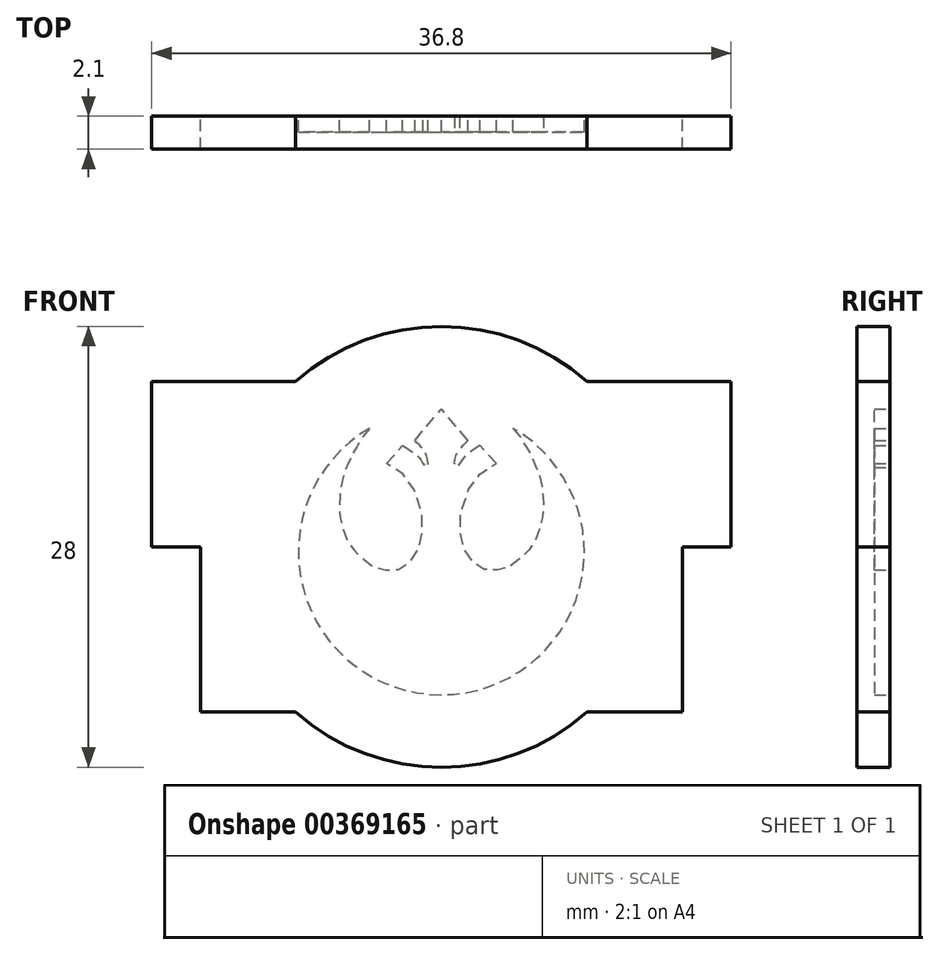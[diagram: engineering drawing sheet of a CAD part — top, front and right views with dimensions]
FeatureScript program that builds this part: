
annotation { "Feature Type Name" : "Feature", "Feature Type Description" : "" }
export const myFeature = defineFeature(function(context is Context, id is Id, definition is map)
    precondition{}
    {
        {
            var Q0;
            Q0=qCreatedBy(makeId("Front.planeOp"),FACE);
            var sketch = newSketch(context, id + "F0", { "sketchPlane" : qUnion([Q0])});
            skArc(sketch, "E0", {"start": v(-9.26, -10.5) * mm, "mid": v(0, -14) * mm, "end": v(9.26, -10.5) * mm});
            skLineSegment(sketch, "E1", {"start": v(9.26, 10.5) * mm, "end": v(18.4, 10.5) * mm});
            skLineSegment(sketch, "E2", {"start": v(18.4, 10.5) * mm, "end": v(18.4, 0) * mm});
            skLineSegment(sketch, "E3", {"start": v(18.4, 0) * mm, "end": v(15.3, 0) * mm});
            skLineSegment(sketch, "E4", {"start": v(15.3, 0) * mm, "end": v(15.3, -10.5) * mm});
            skLineSegment(sketch, "E5", {"start": v(15.3, -10.5) * mm, "end": v(9.26, -10.5) * mm});
            skLineSegment(sketch, "E6.MirrorCS", {"start": v(-18.4, 0) * mm, "end": v(-15.3, 0) * mm});
            skLineSegment(sketch, "E7.MirrorCS", {"start": v(-15.3, 0) * mm, "end": v(-15.3, -10.5) * mm});
            skLineSegment(sketch, "E8.MirrorCS", {"start": v(-9.26, 10.5) * mm, "end": v(-18.4, 10.5) * mm});
            skLineSegment(sketch, "E9.MirrorCS", {"start": v(-18.4, 10.5) * mm, "end": v(-18.4, 0) * mm});
            skLineSegment(sketch, "E10.MirrorCS", {"start": v(-15.3, -10.5) * mm, "end": v(-9.26, -10.5) * mm});
            skArc(sketch, "E11.trimOffspring", {"start": v(9.26, 10.5) * mm, "mid": v(0, 14) * mm, "end": v(-9.26, 10.5) * mm});
            skSolve(sketch);
        }
        {
            var Q0;
            Q0=makeQuery(id+"F0.imprint","IMPRINT",FACE,{"disambiguationData":[TD([[makeQuery(id+"F0.imprint","IMPRINT",EDGE,{"derivedFrom":sQuery(id+"F0.wireOp",EDGE,"E0")}),1.0]])]});
            var sketch = newSketch(context, id + "F1", { "sketchPlane" : qUnion([Q0])});
            skFitSpline(sketch, "E12", {"points": [v(-4.55, 7.53) * mm, v(-4.75, 7.32) * mm, v(-4.96, 7.05) * mm, v(-5.14, 6.75) * mm, v(-5.34, 6.42) * mm, v(-5.51, 6.17) * mm, v(-5.6, 6) * mm, v(-5.74, 5.7) * mm, v(-5.92, 5.26) * mm, v(-6.06, 5) * mm, v(-6.17, 4.68) * mm, v(-6.26, 4.42) * mm, v(-6.34, 4.08) * mm, v(-6.4, 3.7) * mm, v(-6.42, 3.47) * mm, v(-6.44, 3.2) * mm, v(-6.47, 2.88) * mm, v(-6.48, 2.64) * mm, v(-6.47, 2.35) * mm, v(-6.45, 2.01) * mm, v(-6.39, 1.66) * mm, v(-6.3, 1.31) * mm, v(-6.18, 0.91) * mm, v(-6, 0.49) * mm, v(-5.8, 0.11) * mm, v(-5.53, -0.24) * mm, v(-5.2, -0.55) * mm, v(-4.8, -0.92) * mm, v(-4.42, -1.2) * mm, v(-4.07, -1.38) * mm, v(-3.67, -1.47) * mm, v(-3.26, -1.47) * mm, v(-2.72, -1.42) * mm, v(-2.26, -1.2) * mm, v(-1.95, -0.9) * mm, v(-1.53, -0.33) * mm, v(-1.3, 0.4) * mm, v(-1.17, 1.32) * mm, v(-1.31, 2.5) * mm, v(-2.02, 4.17) * mm, v(-2.54, 4.68) * mm, v(-3.49, 5.3) * mm], "startDerivative": vector(-9.97, -9.88) * mm, "endDerivative": vector(-32.17, 18.96) * mm});
            skLineSegment(sketch, "E13", {"start": v(-3.49, 5.3) * mm, "end": v(-2.45, 6.42) * mm});
            skFitSpline(sketch, "E14", {"points": [v(-2.45, 6.42) * mm, v(-1.84, 6.04) * mm, v(-1.38, 5.6) * mm, v(-0.9, 5.05) * mm, v(-1, 5.94) * mm, v(-1.68, 6.77) * mm], "startDerivative": vector(3.54, -2.15) * mm, "endDerivative": vector(-3.1, 4.32) * mm});
            skLineSegment(sketch, "E15", {"start": v(-1.68, 6.77) * mm, "end": v(0, 8.76) * mm});
            skLineSegment(sketch, "E16.MirrorCS", {"start": v(3.49, 5.3) * mm, "end": v(2.45, 6.42) * mm});
            skFitSpline(sketch, "E17.MirrorCS", {"points": [v(2.45, 6.42) * mm, v(1.84, 6.04) * mm, v(1.38, 5.6) * mm, v(0.9, 5.05) * mm, v(1, 5.94) * mm, v(1.68, 6.77) * mm], "startDerivative": vector(-3.54, -2.15) * mm, "endDerivative": vector(3.1, 4.32) * mm});
            skLineSegment(sketch, "E18.MirrorCS", {"start": v(1.68, 6.77) * mm, "end": v(0, 8.76) * mm});
            skFitSpline(sketch, "E19.MirrorCS", {"points": [v(4.55, 7.53) * mm, v(4.75, 7.32) * mm, v(4.96, 7.05) * mm, v(5.14, 6.75) * mm, v(5.34, 6.42) * mm, v(5.51, 6.17) * mm, v(5.6, 6) * mm, v(5.74, 5.7) * mm, v(5.92, 5.26) * mm, v(6.06, 5) * mm, v(6.17, 4.68) * mm, v(6.26, 4.42) * mm, v(6.34, 4.08) * mm, v(6.4, 3.7) * mm, v(6.42, 3.47) * mm, v(6.44, 3.2) * mm, v(6.47, 2.88) * mm, v(6.48, 2.64) * mm, v(6.47, 2.35) * mm, v(6.45, 2.01) * mm, v(6.39, 1.66) * mm, v(6.3, 1.31) * mm, v(6.18, 0.91) * mm, v(6, 0.49) * mm, v(5.8, 0.11) * mm, v(5.53, -0.24) * mm, v(5.2, -0.55) * mm, v(4.8, -0.92) * mm, v(4.42, -1.2) * mm, v(4.07, -1.38) * mm, v(3.67, -1.47) * mm, v(3.26, -1.47) * mm, v(2.72, -1.42) * mm, v(2.26, -1.2) * mm, v(1.95, -0.9) * mm, v(1.53, -0.33) * mm, v(1.3, 0.4) * mm, v(1.17, 1.32) * mm, v(1.31, 2.5) * mm, v(2.02, 4.17) * mm, v(2.54, 4.68) * mm, v(3.49, 5.3) * mm], "startDerivative": vector(9.97, -9.88) * mm, "endDerivative": vector(32.17, 18.96) * mm});
            skArc(sketch, "E20", {"start": v(-4.55, 7.53) * mm, "mid": v(0, -9.4) * mm, "end": v(4.55, 7.53) * mm});
            skSolve(sketch);
        }
        {
            var Q0;
            Q0=makeQuery(id+"F0.imprint","IMPRINT",FACE,{"disambiguationData":[TD([[makeQuery(id+"F0.imprint","IMPRINT",EDGE,{"derivedFrom":sQuery(id+"F0.wireOp",EDGE,"E0")}),1.0]])]});
            extrude(context, id + "F2", {"entities" : qUnion([Q0]), "depth" : 2.1 * mm});
        }
        {
            var Q0;
            Q0=makeQuery(id+"F1.imprint","IMPRINT",FACE,{"disambiguationData":[TD([[makeQuery(id+"F1.imprint","IMPRINT",EDGE,{"derivedFrom":sQuery(id+"F1.wireOp",EDGE,"E12")}),-1.0]])]});
            extrude(context, id + "F3", {"entities" : qUnion([Q0]), "operationType" : NewBodyOperationType.REMOVE, "depth" : 1 * mm});
        }
    });
